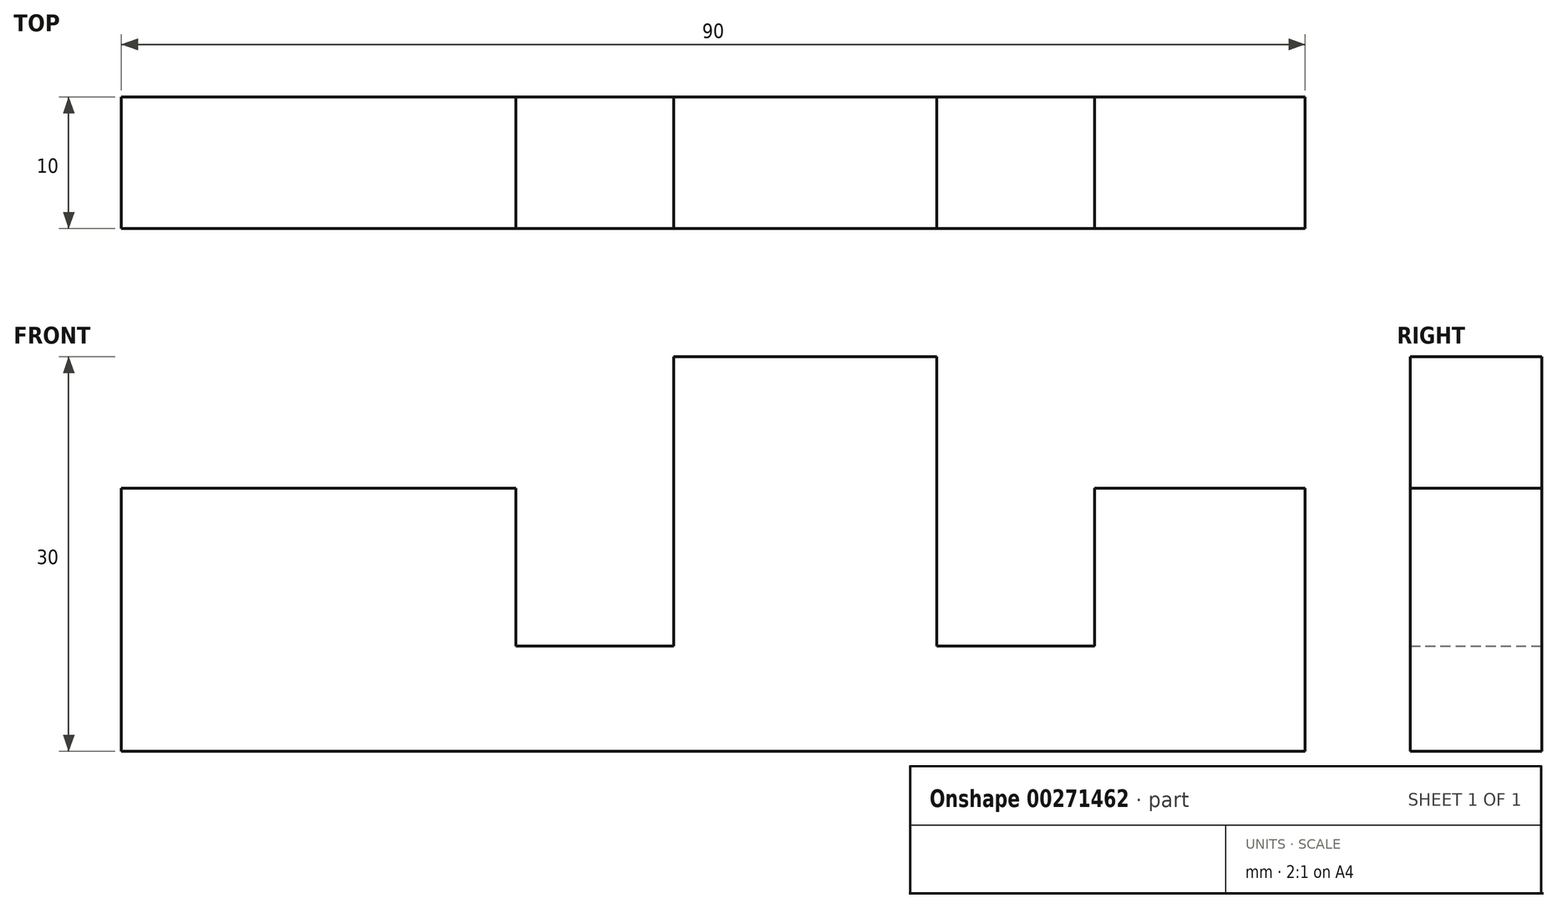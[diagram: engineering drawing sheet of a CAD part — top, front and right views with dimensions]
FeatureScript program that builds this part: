
annotation { "Feature Type Name" : "Feature", "Feature Type Description" : "" }
export const myFeature = defineFeature(function(context is Context, id is Id, definition is map)
    precondition{}
    {
        {
            var Q0;
            Q0=qCreatedBy(makeId("Front.planeOp"),FACE);
            var sketch = newSketch(context, id + "F0", { "sketchPlane" : qUnion([Q0])});
            skLineSegment(sketch, "E0", {"start": v(0, 0) * mm, "end": v(90, 0) * mm});
            skLineSegment(sketch, "E1", {"start": v(0, 0) * mm, "end": v(0, 20) * mm});
            skLineSegment(sketch, "E2", {"start": v(90, 0) * mm, "end": v(90, 20) * mm});
            skLineSegment(sketch, "E3", {"start": v(0, 20) * mm, "end": v(30, 20) * mm});
            skLineSegment(sketch, "E4", {"start": v(30, 20) * mm, "end": v(30, 8) * mm});
            skLineSegment(sketch, "E5", {"start": v(30, 8) * mm, "end": v(42, 8) * mm});
            skLineSegment(sketch, "E6", {"start": v(42, 8) * mm, "end": v(42, 30) * mm});
            skLineSegment(sketch, "E7", {"start": v(42, 30) * mm, "end": v(62, 30) * mm});
            skLineSegment(sketch, "E8", {"start": v(62, 30) * mm, "end": v(62, 8) * mm});
            skLineSegment(sketch, "E9", {"start": v(62, 8) * mm, "end": v(74, 8) * mm});
            skLineSegment(sketch, "E10", {"start": v(74, 8) * mm, "end": v(74, 20) * mm});
            skLineSegment(sketch, "E11", {"start": v(74, 20) * mm, "end": v(90, 20) * mm});
            skSolve(sketch);
        }
        {
            var Q0;
            Q0=makeQuery(id+"F0.imprint","IMPRINT",FACE,{"disambiguationData":[TD([[makeQuery(id+"F0.imprint","IMPRINT",EDGE,{"derivedFrom":sQuery(id+"F0.wireOp",EDGE,"E0")}),1.0]])]});
            extrude(context, id + "F1", {"entities" : qUnion([Q0]), "depth" : 10 * mm});
        }
    });
